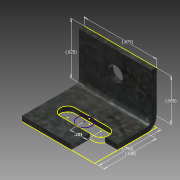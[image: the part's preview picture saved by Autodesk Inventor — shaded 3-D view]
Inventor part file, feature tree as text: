
AUTODESK INVENTOR PART (.ipt)
format: ipt  version: 2015 (Build 190159000, 159)  size: 196,608 bytes
history: native  units: in
note: dims shown in document units (in); Inventor stores cm internally (conversion verified against a paired STEP export)
features: sketch x8, sheet_metal_op x4, other x4, projected_geometry x4, hole x1
ambient origin geometry x8: Origin, YZ Plane, XZ Plane, XY Plane, X Axis, Y Axis, Z Axis, Center Point
bodies: Solid1 (feature_tree)
feature tree (21):
  sheet_metal_op  "Face1"
  sheet_metal_op  "Flange1"
  sketch  "Sketch3"  dims[d3=0.06in]
  hole  "Hole1"  [1 undecoded]
  sketch  "Sketch7"  dims[d5=0.12in]
  sketch  "Sketch8"  dims[d6=0.06in]
  sketch  "Sketch9"  dims[d7=0.625in d8=90.0deg d9=0.06in]
  sketch  "Sketch1"  dims[d0=0.875in d1=0.75in]
  other  "Plate1"
  sketch  "Sketch2"  dims[d2=0.06in]
  other  "Plate2"
  sheet_metal_op  "Bend1"
  sheet_metal_op  "Corner1"
  projected_geometry  "Projected Loop1"
  sketch  "Sketch4"  dims[d4=0.03in]
  projected_geometry  "Projected Loop2"
  projected_geometry  "Projected Loop3"
  projected_geometry  "Projected Loop4"
  sketch  "Sketch10"  dims[d10=0.24in d11=0.06in d12=0.06in d13=0.63in d14=0.875in d15=0.875in d16=0.505in d17=0.177in d18=0.75in d19=0.332in d20=0.25in d21=0.5635in d22=0.06in d23=0.8108in d24=0.177in d25=0.146in d26=0.06in d27=0.0in d28=0.625in d29=0.505in d30=0.875in d31=0.75in d32=0.63in d34=0.203in d35=0.281in d36=0.281in d37=0.281in d38=0.06in d39=0.0in]
  other  "Cut1"
  other  "Cut2"
note: 1 required parameter value undecoded (feature->parameter linkage not recoverable at this tier; creation-order binding heuristic only, values carry confidence <= 0.55)
